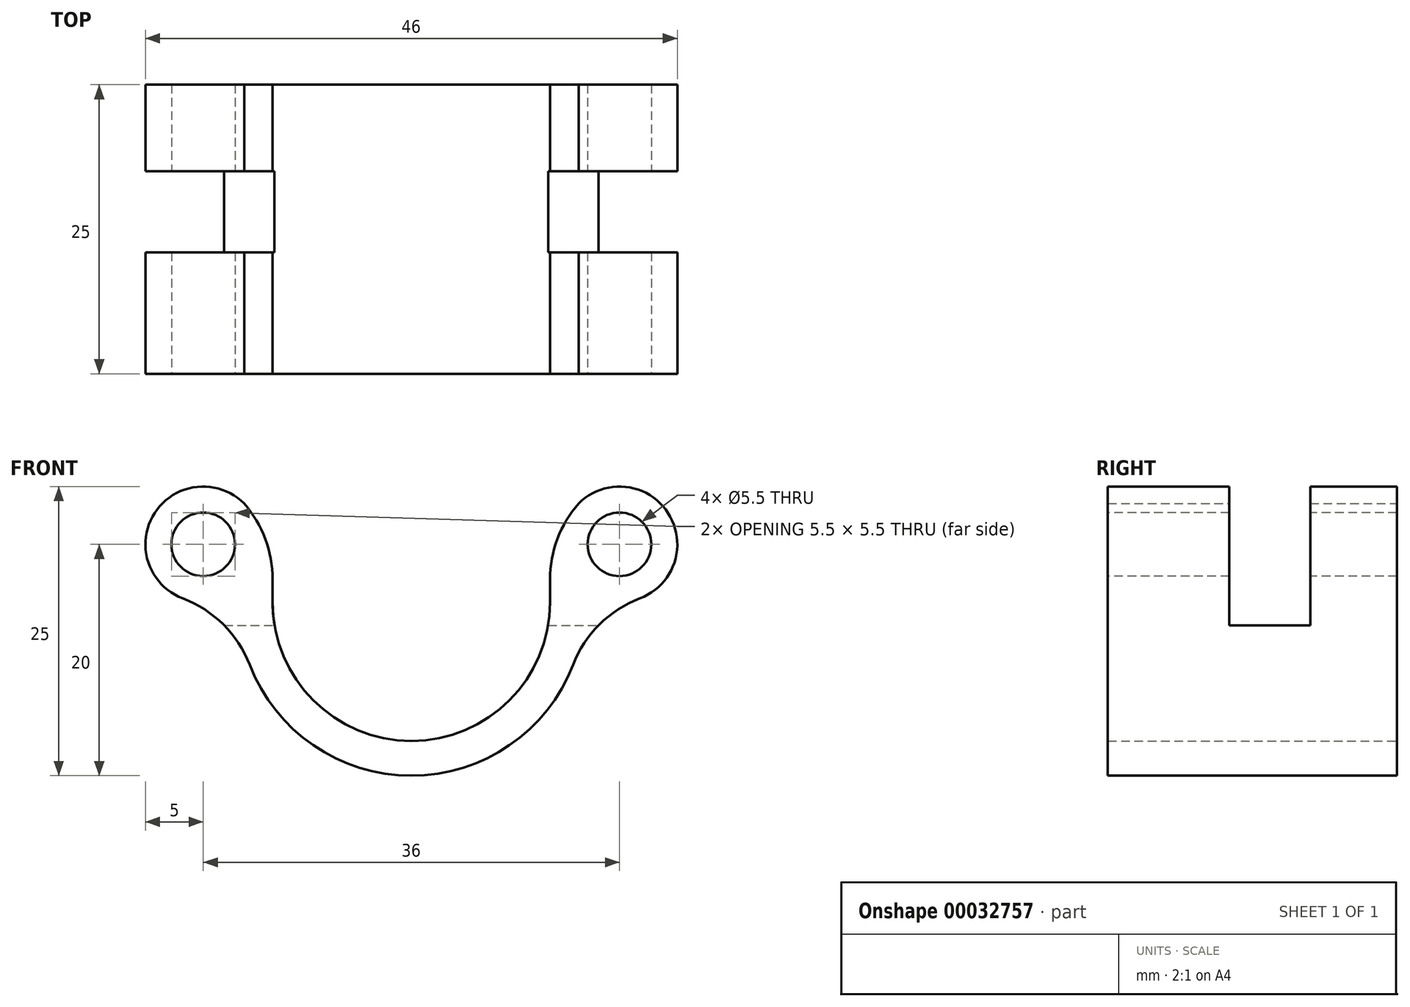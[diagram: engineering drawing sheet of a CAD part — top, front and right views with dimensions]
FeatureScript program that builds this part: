
annotation { "Feature Type Name" : "Feature", "Feature Type Description" : "" }
export const myFeature = defineFeature(function(context is Context, id is Id, definition is map)
    precondition{}
    {
        {
            var Q0;
            Q0=qCreatedBy(makeId("Front.planeOp"),FACE);
            var sketch = newSketch(context, id + "F0", { "sketchPlane" : qUnion([Q0])});
            skArc(sketch, "E0", {"start": v(-12, 0) * mm, "mid": v(0, -12) * mm, "end": v(12, 0) * mm});
            skArc(sketch, "E1", {"start": v(-15, 0) * mm, "mid": v(0, -15) * mm, "end": v(15, 0) * mm});
            skPoint(sketch, "E2", {"position": v(-18, 5) * mm});
            skLineSegment(sketch, "E3", {"start": v(0, 0) * mm, "end": v(0, 10.2) * mm, "construction": true});
            skArc(sketch, "E4", {"start": v(-14.46, 8.54) * mm, "mid": v(-22.62, 6.91) * mm, "end": v(-18, 0) * mm});
            skLineSegment(sketch, "E5", {"start": v(-18, 0) * mm, "end": v(-15, 0) * mm});
            skLineSegment(sketch, "E6", {"start": v(-12, 0) * mm, "end": v(-12, 6.07) * mm});
            skLineSegment(sketch, "E7", {"start": v(-12, 6.07) * mm, "end": v(-14.46, 8.54) * mm});
            skLineSegment(sketch, "E8.MirrorCS", {"start": v(18, 0) * mm, "end": v(15, 0) * mm});
            skPoint(sketch, "E9.MirrorP", {"position": v(18, 5) * mm});
            skLineSegment(sketch, "E10.MirrorCS", {"start": v(12, 0) * mm, "end": v(12, 6.07) * mm});
            skArc(sketch, "E11.MirrorCS", {"start": v(14.46, 8.54) * mm, "mid": v(22.62, 6.91) * mm, "end": v(18, 0) * mm});
            skLineSegment(sketch, "E12.MirrorCS", {"start": v(12, 6.07) * mm, "end": v(14.46, 8.54) * mm});
            skSolve(sketch);
        }
        {
            var Q0;
            Q0 = qSketchRegion(id + "F0", true);
            extrude(context, id + "F1", {"entities" : qUnion([Q0]), "depth" : 12.5 * mm, "hasSecondDirection" : true, "secondDirectionOppositeDirection" : true, "secondDirectionDepth" : 12.5 * mm});
        }
        {
            var Q0;
            Q0=makeQuery(id+"F1.opExtrude","CAP_FACE",FACE,{"disambiguationData":[OSD([sQuery(id+"F0.wireOp",EDGE,"E0"),sQuery(id+"F0.wireOp",EDGE,"E1"),sQuery(id+"F0.wireOp",EDGE,"E4"),sQuery(id+"F0.wireOp",EDGE,"E5"),sQuery(id+"F0.wireOp",EDGE,"E6"),sQuery(id+"F0.wireOp",EDGE,"E7"),sQuery(id+"F0.wireOp",EDGE,"E8.MirrorCS"),sQuery(id+"F0.wireOp",EDGE,"E10.MirrorCS"),sQuery(id+"F0.wireOp",EDGE,"E11.MirrorCS"),sQuery(id+"F0.wireOp",EDGE,"E12.MirrorCS")])],"isStart":false});
            var sketch = newSketch(context, id + "F2", { "sketchPlane" : qUnion([Q0])});
            skPoint(sketch, "E13", {"position": v(-18, 5) * mm});
            skPoint(sketch, "E14", {"position": v(18, 5) * mm});
            skSolve(sketch);
        }
        {
            var Q0;
            Q0=sQuery(id+"F2.wireOp",VERTEX,"E13");
            var Q1;
            Q1=sQuery(id+"F2.wireOp",VERTEX,"E14");
            var Q2;
            Q2=makeQuery(id+"F1.opExtrude","SWEPT_BODY",BODY,{"disambiguationData":[OSD([sQuery(id+"F0.wireOp",EDGE,"E0"),sQuery(id+"F0.wireOp",EDGE,"E1"),sQuery(id+"F0.wireOp",EDGE,"E4"),sQuery(id+"F0.wireOp",EDGE,"E5"),sQuery(id+"F0.wireOp",EDGE,"E6"),sQuery(id+"F0.wireOp",EDGE,"E7"),sQuery(id+"F0.wireOp",EDGE,"E8.MirrorCS"),sQuery(id+"F0.wireOp",EDGE,"E10.MirrorCS"),sQuery(id+"F0.wireOp",EDGE,"E11.MirrorCS"),sQuery(id+"F0.wireOp",EDGE,"E12.MirrorCS")])]});
            hole(context, id + "F3", {"style" : HoleStyle.SIMPLE, "endStyle" : HoleEndStyle.THROUGH, "holeDiameter" : 5.5 * mm, "locations" : qUnion([Q0, Q1]), "scope" : qUnion([Q2]), "isTappedThrough" : true});
        }
        {
            var Q0;
            Q0=makeQuery(id+"F1.opExtrude","SWEPT_EDGE",EDGE,{"disambiguationData":[OSD([sQuery(id+"F0.wireOp",EDGE,"E1"),sQuery(id+"F0.wireOp",EDGE,"E5")])]});
            var Q1;
            Q1=makeQuery(id+"F1.opExtrude","SWEPT_EDGE",EDGE,{"disambiguationData":[OSD([sQuery(id+"F0.wireOp",EDGE,"E1"),sQuery(id+"F0.wireOp",EDGE,"E8.MirrorCS")])]});
            var Q2;
            Q2=makeQuery(id+"F1.opExtrude","SWEPT_EDGE",EDGE,{"disambiguationData":[OSD([sQuery(id+"F0.wireOp",EDGE,"E10.MirrorCS"),sQuery(id+"F0.wireOp",EDGE,"E12.MirrorCS")])]});
            var Q3;
            Q3=makeQuery(id+"F1.opExtrude","SWEPT_EDGE",EDGE,{"disambiguationData":[OSD([sQuery(id+"F0.wireOp",EDGE,"E6"),sQuery(id+"F0.wireOp",EDGE,"E7")])]});
            fillet(context, id + "F4", {"entities" : qUnion([Q0, Q1, Q2, Q3]), "radius" : 10 * mm, "tangentPropagation" : true, "allowEdgeOverflow" : false});
        }
        {
            var Q0;
            Q0=qCreatedBy(makeId("Top.planeOp"),FACE);
            var sketch = newSketch(context, id + "F5", { "sketchPlane" : qUnion([Q0])});
            skLineSegment(sketch, "E15.bottom", {"start": v(-25.73, 5) * mm, "end": v(26.35, 5) * mm});
            skLineSegment(sketch, "E15.top", {"start": v(-25.73, -2) * mm, "end": v(26.35, -2) * mm});
            skLineSegment(sketch, "E15.left", {"start": v(-25.73, 5) * mm, "end": v(-25.73, -2) * mm});
            skLineSegment(sketch, "E15.right", {"start": v(26.35, 5) * mm, "end": v(26.35, -2) * mm});
            skSolve(sketch);
        }
        {
            var Q0;
            Q0 = qSketchRegion(id + "F5", true);
            extrude(context, id + "F6", {"entities" : qUnion([Q0]), "operationType" : NewBodyOperationType.REMOVE, "endBound" : BoundingType.THROUGH_ALL, "depth" : 25 * mm, "hasSecondDirection" : true, "secondDirectionOppositeDirection" : true, "secondDirectionDepth" : 2 * mm});
        }
    });
